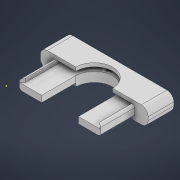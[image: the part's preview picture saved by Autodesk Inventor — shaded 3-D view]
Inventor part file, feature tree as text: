
AUTODESK INVENTOR PART (.ipt)
format: ipt  version: 2022 (Build 260153000, 153)  size: 505,856 bytes
history: native  units: mm
features: sketch x10, extrude x8, fillet x3, emboss x1
ambient origin geometry x8: Origin, YZ Plane, XZ Plane, XY Plane, X Axis, Y Axis, Z Axis, Center Point
bodies: Body1 (feature_tree)
feature tree (22):
  extrude  "Extrusion8"  Depth=10.0mm
  extrude  "Extrusion9"  Depth=20.0mm
  extrude  "Extrusion10"  Depth=35.0mm TaperAngle=0.0deg
  extrude  "Extrusion11"  Depth=63.0mm
  extrude  "Extrusion12"  Depth=2.0mm
  fillet  "Fillet5"  Radius=2.0mm
  extrude  "Extrusion13"  Depth=2.0mm
  fillet  "Fillet6"  Radius=48.0mm
  emboss  "Emboss3"
  sketch  "Sketch22"  dims[d62=1.0mm d63=0.0mm d64=0.2mm d65=0.0mm d66=0.2mm d67=0.0mm]
  extrude  "Extrusion14"  Depth=2.0mm
  extrude  "Extrusion15"  Depth=0.2mm TaperAngle=0.0deg
  fillet  "Fillet7"  Radius=0.2mm
  sketch  "Sketch25"  dims[d69=4.0mm]
  sketch  "Sketch13"  dims[d38=63.0mm d39=10.0mm]
  sketch  "Sketch15"  dims[d40=35.0mm d41=0.0mm d42=20.0mm]
  sketch  "Sketch16"  dims[d43=21.5mm d44=35.0mm d45=0.0mm]
  sketch  "Sketch17"  dims[d46=63.0mm d47=20.0mm]
  sketch  "Sketch19"  dims[d48=2.1mm d49=0.0mm d50=20.0mm d51=2.0mm d52=0.0mm]
  sketch  "Sketch20"  dims[d55=33.0mm d56=0.0mm d57=2.0mm d58=48.0mm]
  sketch  "Sketch21"  dims[d59=20.0mm d60=0.0mm d61=2.0mm]
  sketch  "Sketch23"  dims[d68=2.2mm]
